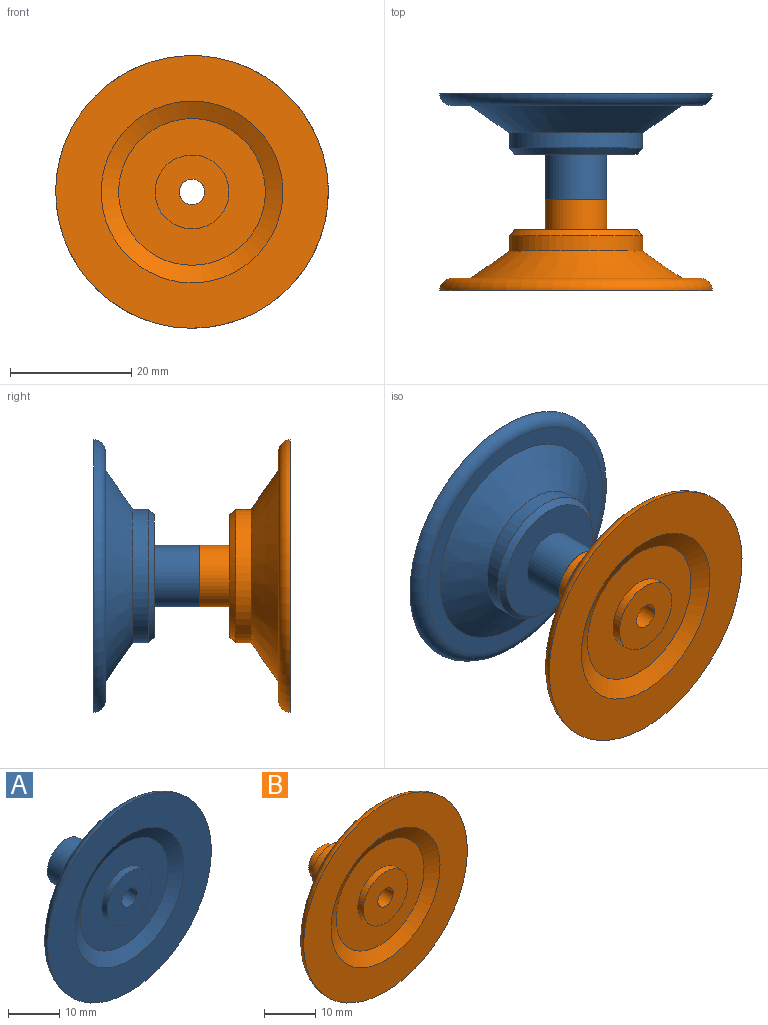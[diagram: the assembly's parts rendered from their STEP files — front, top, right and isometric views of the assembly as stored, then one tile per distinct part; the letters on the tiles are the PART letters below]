
ASSEMBLY  parts=2 mates=1
PART A: 16 faces, bbox 48.7x18.9x48.7 mm
  f0: plane 41x41mm, normal (0,1,0), area 358.1mm2, adj f1,f15
  f1: torus R=20.5mm, axis (0,-1,0), area 429.8mm2, adj f0,f2
  f2: plane 45x45mm, normal (0,-1,0), area 883.6mm2, adj f1,f3
  f3: cone r=12.1mm half-angle=62.7deg, axis (0,-1,0), area 278mm2, adj f2,f4
  f4: plane 24.2x24.2mm, normal (0,-1,0), area 343.1mm2, adj f3,f5
  f5: cylinder r=6.1mm len=12.2mm, axis (0,-1,0), area 57.5mm2, adj f4,f6
  f6: plane 12.2x12.2mm, normal (0,-1,0), area 103mm2, adj f5,f7
  f7: cylinder r=2.1mm len=15mm, axis (0,-1,0), area 197.9mm2, adj f6,f8
  f8: plane 7.4x7.4mm, normal (0,1,0), area 29.2mm2, adj f7,f9
  f9: cylinder r=3.7mm len=7.4mm, axis (0,-1,0), area 58.1mm2, adj f8,f10
  f10: plane 10.2x10.2mm, normal (0,1,0), area 38.7mm2, adj f9,f11
  f11: cylinder r=5.1mm len=10.2mm, axis (0,-1,0), area 240.3mm2, adj f10,f12
  f12: plane 20.2x20.2mm, normal (0,1,0), area 238.8mm2, adj f11,f13
  f13: cone r=10.1mm half-angle=42deg, axis (0,-1,0), area 89.2mm2, adj f12,f14
  f14: cylinder r=11mm len=22mm, axis (0,-1,0), area 172.8mm2, adj f13,f15
  f15: cone r=11mm half-angle=55.3deg, axis (0,-1,0), area 707.8mm2, adj f0,f14
PART B: 16 faces, bbox 48.7x18.9x48.7 mm
  f0: torus R=20.5mm, axis (0,-1,0), area 429.8mm2, adj f1,f15
  f1: plane 45x45mm, normal (0,-1,0), area 883.6mm2, adj f0,f2
  f2: cone r=12.1mm half-angle=62.7deg, axis (0,-1,0), area 278mm2, adj f1,f3
  f3: plane 24.2x24.2mm, normal (0,-1,0), area 343.1mm2, adj f2,f4
  f4: cylinder r=6.1mm len=12.2mm, axis (0,-1,0), area 57.5mm2, adj f3,f5
  f5: plane 12.2x12.2mm, normal (0,-1,0), area 103mm2, adj f4,f6
  f6: cylinder r=2.1mm len=17.5mm, axis (0,-1,0), area 230.9mm2, adj f5,f7
  f7: plane 7.2x7.2mm, normal (0,1,0), area 26.9mm2, adj f6,f8
  f8: cylinder r=3.6mm len=7.2mm, axis (0,-1,0), area 56.5mm2, adj f7,f9
  f9: plane 10.2x10.2mm, normal (0,1,0), area 41mm2, adj f8,f10
  f10: cylinder r=5.1mm len=10.2mm, axis (0,-1,0), area 160.2mm2, adj f9,f11
  f11: plane 20.2x20.2mm, normal (0,1,0), area 238.8mm2, adj f10,f12
  f12: cone r=10.1mm half-angle=42deg, axis (0,-1,0), area 89.2mm2, adj f11,f13
  f13: cylinder r=11mm len=22mm, axis (0,-1,0), area 172.8mm2, adj f12,f14
  f14: cone r=11mm half-angle=55.3deg, axis (0,-1,0), area 707.8mm2, adj f13,f15
  f15: plane 41x41mm, normal (0,1,0), area 358.1mm2, adj f0,f14
PLACE A rot(axis=(0.92,0,0.4),180deg) t=(-14.93,29.84,15)mm
PLACE B rot(axis=(0,1,0),43deg) t=(-14.93,27.34,15)mm
MATE planar B.f0 <-> A.f1  axis (0,1,0) through (-14.93,27.34,15)mm
